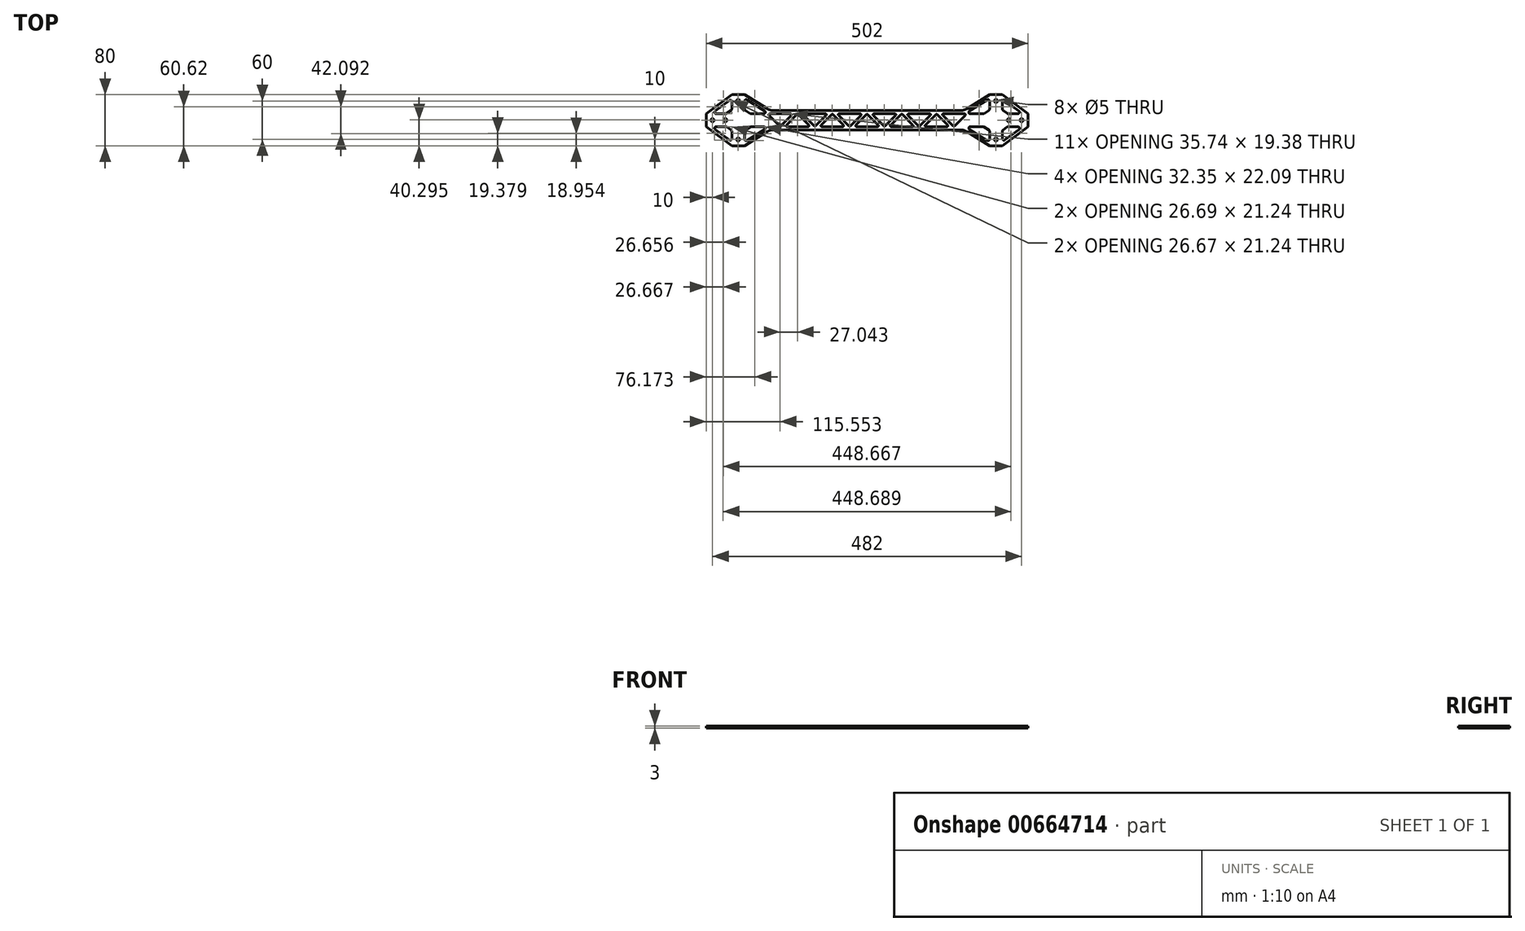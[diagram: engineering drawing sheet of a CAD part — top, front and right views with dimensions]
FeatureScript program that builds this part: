
annotation { "Feature Type Name" : "Feature", "Feature Type Description" : "" }
export const myFeature = defineFeature(function(context is Context, id is Id, definition is map)
    precondition{}
    {
        {
            var Q0;
            Q0=qCreatedBy(makeId("Top.planeOp"),FACE);
            var sketch = newSketch(context, id + "F0", { "sketchPlane" : qUnion([Q0])});
            skLineSegment(sketch, "E0", {"start": v(-92.03, -10) * mm, "end": v(-124.78, -10) * mm});
            skArc(sketch, "E1", {"start": v(-124.78, -10) * mm, "mid": v(-126.17, -9.08) * mm, "end": v(-125.85, -7.44) * mm});
            skLineSegment(sketch, "E2", {"start": v(-125.85, -7.44) * mm, "end": v(-109.46, 8.94) * mm});
            skArc(sketch, "E3", {"start": v(-109.46, 8.94) * mm, "mid": v(-108.4, 9.38) * mm, "end": v(-107.34, 8.94) * mm});
            skLineSegment(sketch, "E4", {"start": v(-107.34, 8.94) * mm, "end": v(-90.97, -7.44) * mm});
            skArc(sketch, "E5", {"start": v(-90.97, -7.44) * mm, "mid": v(-90.64, -9.08) * mm, "end": v(-92.03, -10) * mm});
            skLineSegment(sketch, "E6", {"start": v(-64.98, 9.99) * mm, "end": v(-97.72, 9.99) * mm});
            skArc(sketch, "E7", {"start": v(-97.72, 9.99) * mm, "mid": v(-99.1, 9.06) * mm, "end": v(-98.79, 7.43) * mm});
            skLineSegment(sketch, "E8", {"start": v(-98.79, 7.43) * mm, "end": v(-82.4, -8.95) * mm});
            skArc(sketch, "E9", {"start": v(-82.4, -8.95) * mm, "mid": v(-81.35, -9.4) * mm, "end": v(-80.29, -8.96) * mm});
            skLineSegment(sketch, "E10", {"start": v(-80.29, -8.96) * mm, "end": v(-63.91, 7.43) * mm});
            skArc(sketch, "E11", {"start": v(-63.91, 7.43) * mm, "mid": v(-63.59, 9.06) * mm, "end": v(-64.98, 9.99) * mm});
            skLineSegment(sketch, "E12", {"start": v(-37.86, -10) * mm, "end": v(-70.6, -10) * mm});
            skArc(sketch, "E13", {"start": v(-70.6, -10) * mm, "mid": v(-72, -9.07) * mm, "end": v(-71.67, -7.44) * mm});
            skLineSegment(sketch, "E14", {"start": v(-71.67, -7.44) * mm, "end": v(-55.3, 8.94) * mm});
            skArc(sketch, "E15", {"start": v(-55.3, 8.94) * mm, "mid": v(-54.23, 9.38) * mm, "end": v(-53.17, 8.94) * mm});
            skLineSegment(sketch, "E16", {"start": v(-53.17, 8.94) * mm, "end": v(-36.8, -7.44) * mm});
            skArc(sketch, "E17", {"start": v(-36.8, -7.44) * mm, "mid": v(-36.47, -9.07) * mm, "end": v(-37.86, -10) * mm});
            skLineSegment(sketch, "E18", {"start": v(-10.75, 10) * mm, "end": v(-43.5, 10) * mm});
            skArc(sketch, "E19", {"start": v(-43.5, 10) * mm, "mid": v(-44.88, 9.07) * mm, "end": v(-44.55, 7.43) * mm});
            skLineSegment(sketch, "E20", {"start": v(-44.55, 7.43) * mm, "end": v(-28.18, -8.94) * mm});
            skArc(sketch, "E21", {"start": v(-28.18, -8.94) * mm, "mid": v(-27.12, -9.38) * mm, "end": v(-26.06, -8.95) * mm});
            skLineSegment(sketch, "E22", {"start": v(-26.06, -8.95) * mm, "end": v(-9.68, 7.44) * mm});
            skArc(sketch, "E23", {"start": v(-9.68, 7.44) * mm, "mid": v(-9.36, 9.07) * mm, "end": v(-10.75, 10) * mm});
            skLineSegment(sketch, "E24", {"start": v(16.37, -9.99) * mm, "end": v(-16.38, -9.99) * mm});
            skArc(sketch, "E25", {"start": v(-16.38, -9.99) * mm, "mid": v(-17.77, -9.06) * mm, "end": v(-17.44, -7.42) * mm});
            skLineSegment(sketch, "E26", {"start": v(-17.44, -7.42) * mm, "end": v(-1.06, 8.95) * mm});
            skArc(sketch, "E27", {"start": v(-1.06, 8.95) * mm, "mid": v(0, 9.4) * mm, "end": v(1.06, 8.95) * mm});
            skLineSegment(sketch, "E28", {"start": v(1.06, 8.95) * mm, "end": v(17.43, -7.43) * mm});
            skArc(sketch, "E29", {"start": v(17.43, -7.43) * mm, "mid": v(17.76, -9.06) * mm, "end": v(16.37, -9.99) * mm});
            skLineSegment(sketch, "E30", {"start": v(43.46, 9.99) * mm, "end": v(10.71, 9.99) * mm});
            skArc(sketch, "E31", {"start": v(10.71, 9.99) * mm, "mid": v(9.33, 9.07) * mm, "end": v(9.65, 7.43) * mm});
            skLineSegment(sketch, "E32", {"start": v(9.65, 7.43) * mm, "end": v(26.03, -8.95) * mm});
            skArc(sketch, "E33", {"start": v(26.03, -8.95) * mm, "mid": v(27.09, -9.4) * mm, "end": v(28.15, -8.95) * mm});
            skLineSegment(sketch, "E34", {"start": v(28.15, -8.95) * mm, "end": v(44.53, 7.43) * mm});
            skArc(sketch, "E35", {"start": v(44.53, 7.43) * mm, "mid": v(44.85, 9.07) * mm, "end": v(43.46, 9.99) * mm});
            skLineSegment(sketch, "E36", {"start": v(36.69, -7.44) * mm, "end": v(53.07, 8.94) * mm});
            skArc(sketch, "E37", {"start": v(53.07, 8.94) * mm, "mid": v(54.13, 9.38) * mm, "end": v(55.2, 8.95) * mm});
            skLineSegment(sketch, "E38", {"start": v(55.2, 8.95) * mm, "end": v(71.57, -7.44) * mm});
            skArc(sketch, "E39", {"start": v(71.57, -7.44) * mm, "mid": v(71.9, -9.07) * mm, "end": v(70.51, -10) * mm});
            skLineSegment(sketch, "E40", {"start": v(70.51, -10) * mm, "end": v(37.75, -10) * mm});
            skArc(sketch, "E41", {"start": v(37.75, -10) * mm, "mid": v(36.37, -9.07) * mm, "end": v(36.69, -7.44) * mm});
            skLineSegment(sketch, "E42", {"start": v(63.75, 7.44) * mm, "end": v(80.13, -8.95) * mm});
            skArc(sketch, "E43", {"start": v(80.13, -8.95) * mm, "mid": v(81.19, -9.39) * mm, "end": v(82.25, -8.95) * mm});
            skLineSegment(sketch, "E44", {"start": v(82.25, -8.95) * mm, "end": v(98.63, 7.43) * mm});
            skArc(sketch, "E45", {"start": v(98.63, 7.43) * mm, "mid": v(98.95, 9.07) * mm, "end": v(97.56, 10) * mm});
            skLineSegment(sketch, "E46", {"start": v(97.56, 10) * mm, "end": v(64.81, 10) * mm});
            skArc(sketch, "E47", {"start": v(64.81, 10) * mm, "mid": v(63.43, 9.07) * mm, "end": v(63.75, 7.44) * mm});
            skLineSegment(sketch, "E48", {"start": v(90.86, -7.44) * mm, "end": v(107.24, 8.95) * mm});
            skArc(sketch, "E49", {"start": v(107.24, 8.95) * mm, "mid": v(108.3, 9.39) * mm, "end": v(109.36, 8.95) * mm});
            skLineSegment(sketch, "E50", {"start": v(109.36, 8.95) * mm, "end": v(125.74, -7.43) * mm});
            skArc(sketch, "E51", {"start": v(125.74, -7.43) * mm, "mid": v(126.07, -9.06) * mm, "end": v(124.69, -10) * mm});
            skLineSegment(sketch, "E52", {"start": v(124.69, -10) * mm, "end": v(91.93, -10) * mm});
            skArc(sketch, "E53", {"start": v(91.93, -10) * mm, "mid": v(90.54, -9.07) * mm, "end": v(90.86, -7.44) * mm});
            skLineSegment(sketch, "E54", {"start": v(117.97, 7.44) * mm, "end": v(134.36, -8.94) * mm});
            skArc(sketch, "E55", {"start": v(134.36, -8.94) * mm, "mid": v(135.42, -9.38) * mm, "end": v(136.48, -8.94) * mm});
            skLineSegment(sketch, "E56", {"start": v(136.48, -8.94) * mm, "end": v(152.85, 7.44) * mm});
            skArc(sketch, "E57", {"start": v(152.85, 7.44) * mm, "mid": v(153.18, 9.08) * mm, "end": v(151.79, 10) * mm});
            skLineSegment(sketch, "E58", {"start": v(151.79, 10) * mm, "end": v(119.04, 10) * mm});
            skArc(sketch, "E59", {"start": v(119.04, 10) * mm, "mid": v(117.66, 9.08) * mm, "end": v(117.97, 7.44) * mm});
            skLineSegment(sketch, "E60", {"start": v(-119.06, 9.98) * mm, "end": v(-151.82, 9.98) * mm});
            skArc(sketch, "E61", {"start": v(-151.82, 9.98) * mm, "mid": v(-153.21, 9.06) * mm, "end": v(-152.88, 7.42) * mm});
            skLineSegment(sketch, "E62", {"start": v(-152.88, 7.42) * mm, "end": v(-136.5, -8.95) * mm});
            skArc(sketch, "E63", {"start": v(-136.5, -8.95) * mm, "mid": v(-135.45, -9.4) * mm, "end": v(-134.39, -8.96) * mm});
            skLineSegment(sketch, "E64", {"start": v(-134.39, -8.96) * mm, "end": v(-118, 7.42) * mm});
            skArc(sketch, "E65", {"start": v(-118, 7.42) * mm, "mid": v(-117.68, 9.06) * mm, "end": v(-119.06, 9.98) * mm});
            skArc(sketch, "E66", {"start": v(241, 2.5) * mm, "mid": v(242.77, 1.77) * mm, "end": v(243.5, 0) * mm});
            skArc(sketch, "E67", {"start": v(243.5, 0) * mm, "mid": v(242.77, -1.77) * mm, "end": v(241, -2.5) * mm});
            skArc(sketch, "E68", {"start": v(241, -2.5) * mm, "mid": v(239.23, -1.77) * mm, "end": v(238.5, 0) * mm});
            skArc(sketch, "E69", {"start": v(238.5, 0) * mm, "mid": v(239.23, 1.77) * mm, "end": v(241, 2.5) * mm});
            skArc(sketch, "E70", {"start": v(221, 2.5) * mm, "mid": v(222.77, 1.77) * mm, "end": v(223.5, 0) * mm});
            skArc(sketch, "E71", {"start": v(223.5, 0) * mm, "mid": v(222.77, -1.77) * mm, "end": v(221, -2.5) * mm});
            skArc(sketch, "E72", {"start": v(221, -2.5) * mm, "mid": v(219.23, -1.77) * mm, "end": v(218.5, 0) * mm});
            skArc(sketch, "E73", {"start": v(218.5, 0) * mm, "mid": v(219.23, 1.77) * mm, "end": v(221, 2.5) * mm});
            skArc(sketch, "E74", {"start": v(201, 32.5) * mm, "mid": v(202.77, 31.77) * mm, "end": v(203.5, 30) * mm});
            skArc(sketch, "E75", {"start": v(203.5, 30) * mm, "mid": v(202.77, 28.23) * mm, "end": v(201, 27.5) * mm});
            skArc(sketch, "E76", {"start": v(201, 27.5) * mm, "mid": v(199.23, 28.23) * mm, "end": v(198.5, 30) * mm});
            skArc(sketch, "E77", {"start": v(198.5, 30) * mm, "mid": v(199.23, 31.77) * mm, "end": v(201, 32.5) * mm});
            skArc(sketch, "E78", {"start": v(201, -27.5) * mm, "mid": v(202.77, -28.23) * mm, "end": v(203.5, -30) * mm});
            skArc(sketch, "E79", {"start": v(203.5, -30) * mm, "mid": v(202.77, -31.77) * mm, "end": v(201, -32.5) * mm});
            skArc(sketch, "E80", {"start": v(201, -32.5) * mm, "mid": v(199.23, -31.77) * mm, "end": v(198.5, -30) * mm});
            skArc(sketch, "E81", {"start": v(198.5, -30) * mm, "mid": v(199.23, -28.23) * mm, "end": v(201, -27.5) * mm});
            skLineSegment(sketch, "E82", {"start": v(215, -30.75) * mm, "end": v(236.69, -14.5) * mm});
            skArc(sketch, "E83", {"start": v(236.69, -14.5) * mm, "mid": v(237.56, -11.7) * mm, "end": v(235.18, -10) * mm});
            skLineSegment(sketch, "E84", {"start": v(235.18, -10) * mm, "end": v(220.13, -10) * mm});
            skArc(sketch, "E85", {"start": v(220.13, -10) * mm, "mid": v(219.34, -10.13) * mm, "end": v(218.64, -10.5) * mm});
            skArc(sketch, "E86", {"start": v(218.64, -10.5) * mm, "mid": v(218.63, -10.5) * mm, "end": v(218.63, -10.5) * mm});
            skLineSegment(sketch, "E87", {"start": v(218.63, -10.5) * mm, "end": v(212, -15.48) * mm});
            skArc(sketch, "E88", {"start": v(212, -15.48) * mm, "mid": v(211.26, -16.37) * mm, "end": v(211, -17.5) * mm});
            skLineSegment(sketch, "E89", {"start": v(211, -17.5) * mm, "end": v(211, -28.75) * mm});
            skArc(sketch, "E90", {"start": v(211, -28.75) * mm, "mid": v(212.39, -31) * mm, "end": v(215, -30.75) * mm});
            skLineSegment(sketch, "E91", {"start": v(218.65, 10.5) * mm, "end": v(212, 15.5) * mm});
            skArc(sketch, "E92", {"start": v(212, 15.5) * mm, "mid": v(211.26, 16.39) * mm, "end": v(211, 17.51) * mm});
            skLineSegment(sketch, "E93", {"start": v(211, 17.51) * mm, "end": v(211, 28.75) * mm});
            skArc(sketch, "E94", {"start": v(211, 28.75) * mm, "mid": v(212.38, 30.98) * mm, "end": v(215, 30.76) * mm});
            skLineSegment(sketch, "E95", {"start": v(215, 30.76) * mm, "end": v(236.67, 14.5) * mm});
            skArc(sketch, "E96", {"start": v(236.67, 14.5) * mm, "mid": v(237.54, 11.7) * mm, "end": v(235.17, 10) * mm});
            skLineSegment(sketch, "E97", {"start": v(235.17, 10) * mm, "end": v(220.16, 10) * mm});
            skArc(sketch, "E98", {"start": v(220.16, 10) * mm, "mid": v(219.37, 10.13) * mm, "end": v(218.65, 10.5) * mm});
            skLineSegment(sketch, "E99", {"start": v(161.15, 10) * mm, "end": v(180.86, 10) * mm});
            skArc(sketch, "E100", {"start": v(180.86, 10) * mm, "mid": v(181.54, 10.1) * mm, "end": v(182.17, 10.37) * mm});
            skLineSegment(sketch, "E101", {"start": v(182.17, 10.37) * mm, "end": v(189.82, 15.16) * mm});
            skArc(sketch, "E102", {"start": v(189.82, 15.16) * mm, "mid": v(190.69, 16.06) * mm, "end": v(191, 17.28) * mm});
            skLineSegment(sketch, "E103", {"start": v(191, 17.28) * mm, "end": v(191, 29.6) * mm});
            skArc(sketch, "E104", {"start": v(191, 29.6) * mm, "mid": v(189.71, 31.78) * mm, "end": v(187.18, 31.72) * mm});
            skLineSegment(sketch, "E105", {"start": v(187.18, 31.72) * mm, "end": v(159.83, 14.63) * mm});
            skArc(sketch, "E106", {"start": v(159.83, 14.63) * mm, "mid": v(158.75, 11.82) * mm, "end": v(161.15, 10) * mm});
            skLineSegment(sketch, "E107", {"start": v(181.56, -10) * mm, "end": v(161.15, -10) * mm});
            skArc(sketch, "E108", {"start": v(161.15, -10) * mm, "mid": v(158.75, -11.81) * mm, "end": v(159.83, -14.62) * mm});
            skLineSegment(sketch, "E109", {"start": v(159.83, -14.62) * mm, "end": v(187.18, -31.71) * mm});
            skArc(sketch, "E110", {"start": v(187.18, -31.71) * mm, "mid": v(189.72, -31.78) * mm, "end": v(191, -29.58) * mm});
            skLineSegment(sketch, "E111", {"start": v(191, -29.58) * mm, "end": v(191, -17.28) * mm});
            skArc(sketch, "E112", {"start": v(191, -17.28) * mm, "mid": v(190.68, -16.06) * mm, "end": v(189.82, -15.16) * mm});
            skLineSegment(sketch, "E113", {"start": v(189.82, -15.16) * mm, "end": v(181.56, -10) * mm});
            skArc(sketch, "E114", {"start": v(-241, 2.5) * mm, "mid": v(-242.77, 1.77) * mm, "end": v(-243.5, 0) * mm});
            skArc(sketch, "E115", {"start": v(-243.5, 0) * mm, "mid": v(-242.77, -1.77) * mm, "end": v(-241, -2.5) * mm});
            skArc(sketch, "E116", {"start": v(-241, -2.5) * mm, "mid": v(-239.23, -1.77) * mm, "end": v(-238.5, 0) * mm});
            skArc(sketch, "E117", {"start": v(-238.5, 0) * mm, "mid": v(-239.23, 1.77) * mm, "end": v(-241, 2.5) * mm});
            skArc(sketch, "E118", {"start": v(-221, 2.5) * mm, "mid": v(-222.77, 1.77) * mm, "end": v(-223.5, 0) * mm});
            skArc(sketch, "E119", {"start": v(-223.5, 0) * mm, "mid": v(-222.77, -1.77) * mm, "end": v(-221, -2.5) * mm});
            skArc(sketch, "E120", {"start": v(-221, -2.5) * mm, "mid": v(-219.23, -1.77) * mm, "end": v(-218.5, 0) * mm});
            skArc(sketch, "E121", {"start": v(-218.5, 0) * mm, "mid": v(-219.23, 1.77) * mm, "end": v(-221, 2.5) * mm});
            skArc(sketch, "E122", {"start": v(-201, 32.5) * mm, "mid": v(-202.77, 31.77) * mm, "end": v(-203.5, 30) * mm});
            skArc(sketch, "E123", {"start": v(-203.5, 30) * mm, "mid": v(-202.77, 28.23) * mm, "end": v(-201, 27.5) * mm});
            skArc(sketch, "E124", {"start": v(-201, 27.5) * mm, "mid": v(-199.23, 28.23) * mm, "end": v(-198.5, 30) * mm});
            skArc(sketch, "E125", {"start": v(-198.5, 30) * mm, "mid": v(-199.23, 31.77) * mm, "end": v(-201, 32.5) * mm});
            skArc(sketch, "E126", {"start": v(-201, -27.5) * mm, "mid": v(-202.77, -28.23) * mm, "end": v(-203.5, -30) * mm});
            skArc(sketch, "E127", {"start": v(-203.5, -30) * mm, "mid": v(-202.77, -31.77) * mm, "end": v(-201, -32.5) * mm});
            skArc(sketch, "E128", {"start": v(-201, -32.5) * mm, "mid": v(-199.23, -31.77) * mm, "end": v(-198.5, -30) * mm});
            skArc(sketch, "E129", {"start": v(-198.5, -30) * mm, "mid": v(-199.23, -28.23) * mm, "end": v(-201, -27.5) * mm});
            skLineSegment(sketch, "E130", {"start": v(-215, -30.75) * mm, "end": v(-236.69, -14.5) * mm});
            skArc(sketch, "E131", {"start": v(-236.69, -14.5) * mm, "mid": v(-237.56, -11.7) * mm, "end": v(-235.18, -10) * mm});
            skLineSegment(sketch, "E132", {"start": v(-235.18, -10) * mm, "end": v(-220.13, -10) * mm});
            skArc(sketch, "E133", {"start": v(-220.13, -10) * mm, "mid": v(-219.34, -10.13) * mm, "end": v(-218.64, -10.5) * mm});
            skArc(sketch, "E134", {"start": v(-218.64, -10.5) * mm, "mid": v(-218.63, -10.5) * mm, "end": v(-218.63, -10.5) * mm});
            skLineSegment(sketch, "E135", {"start": v(-218.63, -10.5) * mm, "end": v(-212, -15.48) * mm});
            skArc(sketch, "E136", {"start": v(-212, -15.48) * mm, "mid": v(-211.26, -16.37) * mm, "end": v(-211, -17.5) * mm});
            skLineSegment(sketch, "E137", {"start": v(-211, -17.5) * mm, "end": v(-211, -28.75) * mm});
            skArc(sketch, "E138", {"start": v(-211, -28.75) * mm, "mid": v(-212.39, -31) * mm, "end": v(-215, -30.75) * mm});
            skLineSegment(sketch, "E139", {"start": v(-218.65, 10.5) * mm, "end": v(-212, 15.5) * mm});
            skArc(sketch, "E140", {"start": v(-212, 15.5) * mm, "mid": v(-211.26, 16.39) * mm, "end": v(-211, 17.51) * mm});
            skLineSegment(sketch, "E141", {"start": v(-211, 17.51) * mm, "end": v(-211, 28.75) * mm});
            skArc(sketch, "E142", {"start": v(-211, 28.75) * mm, "mid": v(-212.38, 30.98) * mm, "end": v(-215, 30.76) * mm});
            skLineSegment(sketch, "E143", {"start": v(-215, 30.76) * mm, "end": v(-236.67, 14.5) * mm});
            skArc(sketch, "E144", {"start": v(-236.67, 14.5) * mm, "mid": v(-237.54, 11.7) * mm, "end": v(-235.17, 10) * mm});
            skLineSegment(sketch, "E145", {"start": v(-235.17, 10) * mm, "end": v(-220.16, 10) * mm});
            skArc(sketch, "E146", {"start": v(-220.16, 10) * mm, "mid": v(-219.37, 10.13) * mm, "end": v(-218.65, 10.5) * mm});
            skLineSegment(sketch, "E147", {"start": v(-161.15, 10) * mm, "end": v(-180.86, 10) * mm});
            skArc(sketch, "E148", {"start": v(-180.86, 10) * mm, "mid": v(-181.54, 10.1) * mm, "end": v(-182.17, 10.37) * mm});
            skLineSegment(sketch, "E149", {"start": v(-182.17, 10.37) * mm, "end": v(-189.82, 15.16) * mm});
            skArc(sketch, "E150", {"start": v(-189.82, 15.16) * mm, "mid": v(-190.69, 16.06) * mm, "end": v(-191, 17.28) * mm});
            skLineSegment(sketch, "E151", {"start": v(-191, 17.28) * mm, "end": v(-191, 29.6) * mm});
            skArc(sketch, "E152", {"start": v(-191, 29.6) * mm, "mid": v(-189.71, 31.78) * mm, "end": v(-187.18, 31.72) * mm});
            skLineSegment(sketch, "E153", {"start": v(-187.18, 31.72) * mm, "end": v(-159.83, 14.63) * mm});
            skArc(sketch, "E154", {"start": v(-159.83, 14.63) * mm, "mid": v(-158.75, 11.82) * mm, "end": v(-161.15, 10) * mm});
            skLineSegment(sketch, "E155", {"start": v(-181.56, -10) * mm, "end": v(-161.15, -10) * mm});
            skArc(sketch, "E156", {"start": v(-161.15, -10) * mm, "mid": v(-158.75, -11.81) * mm, "end": v(-159.83, -14.62) * mm});
            skLineSegment(sketch, "E157", {"start": v(-159.83, -14.62) * mm, "end": v(-187.18, -31.71) * mm});
            skArc(sketch, "E158", {"start": v(-187.18, -31.71) * mm, "mid": v(-189.72, -31.78) * mm, "end": v(-191, -29.58) * mm});
            skLineSegment(sketch, "E159", {"start": v(-191, -29.58) * mm, "end": v(-191, -17.28) * mm});
            skArc(sketch, "E160", {"start": v(-191, -17.28) * mm, "mid": v(-190.68, -16.06) * mm, "end": v(-189.82, -15.16) * mm});
            skLineSegment(sketch, "E161", {"start": v(-189.82, -15.16) * mm, "end": v(-181.56, -10) * mm});
            skLineSegment(sketch, "E162", {"start": v(-191, -40) * mm, "end": v(-155.86, -18.04) * mm});
            skArc(sketch, "E163", {"start": v(-155.86, -18.04) * mm, "mid": v(-150.74, -15.76) * mm, "end": v(-145.2, -15) * mm});
            skLineSegment(sketch, "E164", {"start": v(-145.2, -15) * mm, "end": v(145.26, -15) * mm});
            skArc(sketch, "E165", {"start": v(145.26, -15) * mm, "mid": v(150.74, -15.76) * mm, "end": v(155.8, -18) * mm});
            skLineSegment(sketch, "E166", {"start": v(155.8, -18) * mm, "end": v(191, -40) * mm});
            skLineSegment(sketch, "E167", {"start": v(191, -40) * mm, "end": v(211, -40) * mm});
            skLineSegment(sketch, "E168", {"start": v(211, -40) * mm, "end": v(251, -10) * mm});
            skLineSegment(sketch, "E169", {"start": v(251, -10) * mm, "end": v(251, 10) * mm});
            skLineSegment(sketch, "E170", {"start": v(251, 10) * mm, "end": v(211, 40) * mm});
            skLineSegment(sketch, "E171", {"start": v(211, 40) * mm, "end": v(191, 40) * mm});
            skLineSegment(sketch, "E172", {"start": v(191, 40) * mm, "end": v(155.86, 18.04) * mm});
            skArc(sketch, "E173", {"start": v(155.86, 18.04) * mm, "mid": v(150.74, 15.76) * mm, "end": v(145.18, 15) * mm});
            skLineSegment(sketch, "E174", {"start": v(145.18, 15) * mm, "end": v(-145.26, 15) * mm});
            skArc(sketch, "E175", {"start": v(-145.26, 15) * mm, "mid": v(-150.82, 15.79) * mm, "end": v(-155.93, 18.08) * mm});
            skLineSegment(sketch, "E176", {"start": v(-155.93, 18.08) * mm, "end": v(-191, 40) * mm});
            skLineSegment(sketch, "E177", {"start": v(-191, 40) * mm, "end": v(-211, 40) * mm});
            skLineSegment(sketch, "E178", {"start": v(-211, 40) * mm, "end": v(-251, 10) * mm});
            skLineSegment(sketch, "E179", {"start": v(-251, 10) * mm, "end": v(-251, -10) * mm});
            skLineSegment(sketch, "E180", {"start": v(-251, -10) * mm, "end": v(-211, -40) * mm});
            skLineSegment(sketch, "E181", {"start": v(-211, -40) * mm, "end": v(-191, -40) * mm});
            skSolve(sketch);
        }
        {
            var Q0;
            Q0=makeQuery(id+"F0.imprint","IMPRINT",FACE,{"disambiguationData":[TD([[makeQuery(id+"F0.imprint","IMPRINT",EDGE,{"derivedFrom":sQuery(id+"F0.wireOp",EDGE,"E0")}),1.0]])]});
            extrude(context, id + "F1", {"entities" : qUnion([Q0]), "depth" : 3 * mm, "offsetDistance" : 25 * mm});
        }
    });
